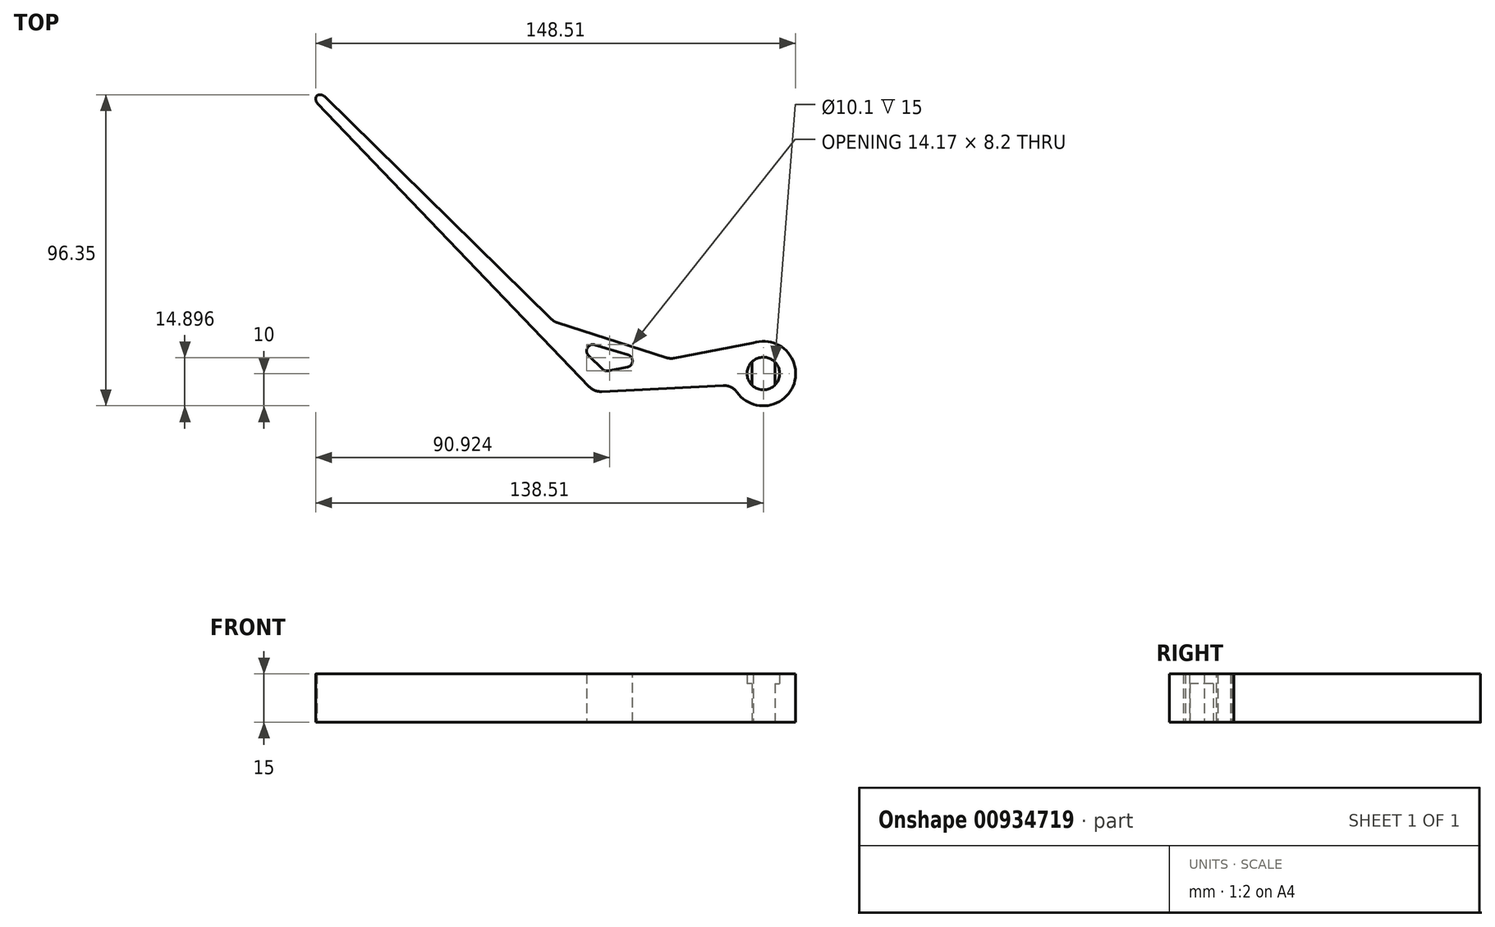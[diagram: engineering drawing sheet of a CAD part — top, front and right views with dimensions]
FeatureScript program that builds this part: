
annotation { "Feature Type Name" : "Feature", "Feature Type Description" : "" }
export const myFeature = defineFeature(function(context is Context, id is Id, definition is map)
    precondition{}
    {
        {
            var Q0;
            Q0=qCreatedBy(makeId("Top.planeOp"),FACE);
            var sketch = newSketch(context, id + "F0", { "sketchPlane" : qUnion([Q0])});
            skCircle(sketch, "E0", {"center": v(0, 0) * mm, "radius": 5.05 * mm});
            skLineSegment(sketch, "E1", {"start": v(-3.55, 3.6) * mm, "end": v(-3.55, -3.6) * mm});
            skLineSegment(sketch, "E2", {"start": v(3.55, 3.6) * mm, "end": v(3.55, -3.6) * mm});
            skCircle(sketch, "E3", {"center": v(0, 0) * mm, "radius": 10 * mm});
            skLineSegment(sketch, "E4", {"start": v(-3.14, 9.5) * mm, "end": v(-49.06, 0.63) * mm});
            skLineSegment(sketch, "E5", {"start": v(-9.33, -3.6) * mm, "end": v(-52.33, -5.7) * mm});
            skLineSegment(sketch, "E6", {"start": v(-52.33, -5.7) * mm, "end": v(-139.34, 85.06) * mm});
            skLineSegment(sketch, "E7", {"start": v(-139.34, 85.06) * mm, "end": v(-137.18, 87.13) * mm});
            skLineSegment(sketch, "E8", {"start": v(-137.18, 87.13) * mm, "end": v(-49.06, 0.63) * mm});
            skPoint(sketch, "E9.orphan", {"position": v(-52.33, 0) * mm});
            skLineSegment(sketch, "E10", {"start": v(-59.87, 11.24) * mm, "end": v(-34.14, 3.51) * mm});
            skLineSegment(sketch, "E11", {"start": v(-28.82, 4.54) * mm, "end": v(-64.76, 16.05) * mm});
            skSolve(sketch);
        }
        {
            var Q0;
            Q0 = qSketchRegion(id + "F0", true);
            extrude(context, id + "F1", {"entities" : qUnion([Q0]), "depth" : 15 * mm, "offsetDistance" : 25 * mm});
        }
        {
            var Q0;
            {var subQ0=sQuery(id+"F0.wireOp",EDGE,"E1");Q0=makeQuery(id+"F0.imprint","IMPRINT",FACE,{"disambiguationData":[TD([[makeQuery(id+"F0.imprint","IMPRINT",EDGE,{"derivedFrom":subQ0}),-1.0]])]});}
            var Q1;
            {var subQ0=sQuery(id+"F0.wireOp",EDGE,"E2");Q1=makeQuery(id+"F0.imprint","IMPRINT",FACE,{"disambiguationData":[TD([[makeQuery(id+"F0.imprint","IMPRINT",EDGE,{"derivedFrom":subQ0}),1.0]])]});}
            extrude(context, id + "F2", {"entities" : qUnion([Q0, Q1]), "operationType" : NewBodyOperationType.ADD, "depth" : 12 * mm, "offsetDistance" : 25 * mm});
        }
        {
            var Q0;
            Q0=makeQuery(id+"F1.opExtrude","SWEPT_EDGE",EDGE,{"disambiguationData":[OSD([sQuery(id+"F0.wireOp",EDGE,"E5"),sQuery(id+"F0.wireOp",EDGE,"E6")])]});
            var Q1;
            Q1=makeQuery(id+"F1.opExtrude","SWEPT_EDGE",EDGE,{"disambiguationData":[OSD([sQuery(id+"F0.wireOp",EDGE,"E3"),sQuery(id+"F0.wireOp",EDGE,"E5")])]});
            var Q2;
            Q2=makeQuery(id+"F1.opExtrude","SWEPT_EDGE",EDGE,{"disambiguationData":[OSD([sQuery(id+"F0.wireOp",EDGE,"E8"),sQuery(id+"F0.wireOp",EDGE,"E11")])]});
            var Q3;
            Q3=makeQuery(id+"F1.opExtrude","SWEPT_EDGE",EDGE,{"disambiguationData":[OSD([sQuery(id+"F0.wireOp",EDGE,"E4"),sQuery(id+"F0.wireOp",EDGE,"E11")])]});
            fillet(context, id + "F3", {"entities" : qUnion([Q0, Q1, Q2, Q3]), "radius" : 5 * mm, "tangentPropagation" : true, "allowEdgeOverflow" : false});
        }
        {
            var Q0;
            Q0=makeQuery(id+"F1.opExtrude","SWEPT_EDGE",EDGE,{"disambiguationData":[OSD([sQuery(id+"F0.wireOp",EDGE,"E6"),sQuery(id+"F0.wireOp",EDGE,"E7")])]});
            var Q1;
            Q1=makeQuery(id+"F1.opExtrude","SWEPT_EDGE",EDGE,{"disambiguationData":[OSD([sQuery(id+"F0.wireOp",EDGE,"E8"),sQuery(id+"F0.wireOp",EDGE,"E10")])]});
            var Q2;
            Q2=makeQuery(id+"F1.opExtrude","SWEPT_EDGE",EDGE,{"disambiguationData":[OSD([sQuery(id+"F0.wireOp",EDGE,"E4"),sQuery(id+"F0.wireOp",EDGE,"E10")])]});
            var Q3;
            Q3=makeQuery(id+"F1.opExtrude","SWEPT_EDGE",EDGE,{"disambiguationData":[OSD([sQuery(id+"F0.wireOp",EDGE,"E4"),sQuery(id+"F0.wireOp",EDGE,"E8")])]});
            var Q4;
            Q4=makeQuery(id+"F1.opExtrude","SWEPT_EDGE",EDGE,{"disambiguationData":[OSD([sQuery(id+"F0.wireOp",EDGE,"E7"),sQuery(id+"F0.wireOp",EDGE,"E8")])]});
            fillet(context, id + "F4", {"entities" : qUnion([Q0, Q1, Q2, Q3, Q4]), "radius" : 2 * mm, "tangentPropagation" : true, "allowEdgeOverflow" : false});
        }
    });
